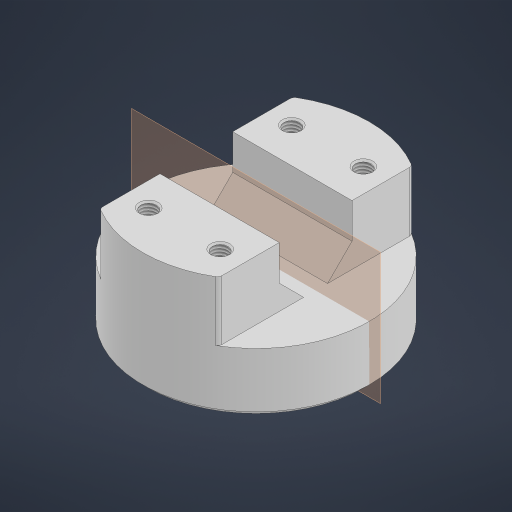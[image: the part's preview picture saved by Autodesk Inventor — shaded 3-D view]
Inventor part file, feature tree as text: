
AUTODESK INVENTOR PART (.ipt)
format: ipt  version: 2024.3 (Build 283343000, 343)  size: 460,288 bytes
history: native  units: mm
features: sketch x5, extrude x3, hole x1, fillet x1, chamfer x1, other x1, projected_geometry x1
ambient origin geometry x8: Origin, YZ Plane, XZ Plane, XY Plane, X Axis, Y Axis, Z Axis, Center Point
bodies: Solid1 (feature_tree)
feature tree (13):
  extrude  "Extrusion1"  Depth=50.0mm TaperAngle=0.0deg
  extrude  "Extrusion3"  TaperAngle=45.0deg  [1 undecoded]
  extrude  "Extrusion4"  Depth=25.0mm
  hole  "Hole2"  [1 undecoded]
  fillet  "Fillet1"  Radius=10.0mm
  chamfer  "Chamfer3"  Distance=60.0mm
  other  "Mark1"
  sketch  "Sketch1"  dims[d0=95.0mm d1=50.0mm d2=0.0mm]
  sketch  "Sketch4"  dims[d22=30.5mm d23=45.0deg]
  projected_geometry  "Projected Loop1"
  sketch  "Sketch5"  dims[d24=10.0mm d25=25.0mm]
  sketch  "Sketch6"  dims[d26=0.0mm d27=0.0mm d28=50.0mm d29=10.0mm d30=0.0mm]
  sketch  "Sketch7"  dims[d31=30.0mm d32=60.0mm d33=6.647mm d34=16.0mm d35=8.0mm d36=2.0mm d37=90.0deg d38=20.4mm d39=20.594885mm d40=2.0mm d41=2.0mm d42=2.0mm d43=45.0deg d44=4.0mm d45=30.0mm]
note: 2 required parameter values undecoded (feature->parameter linkage not recoverable at this tier; creation-order binding heuristic only, values carry confidence <= 0.55)
